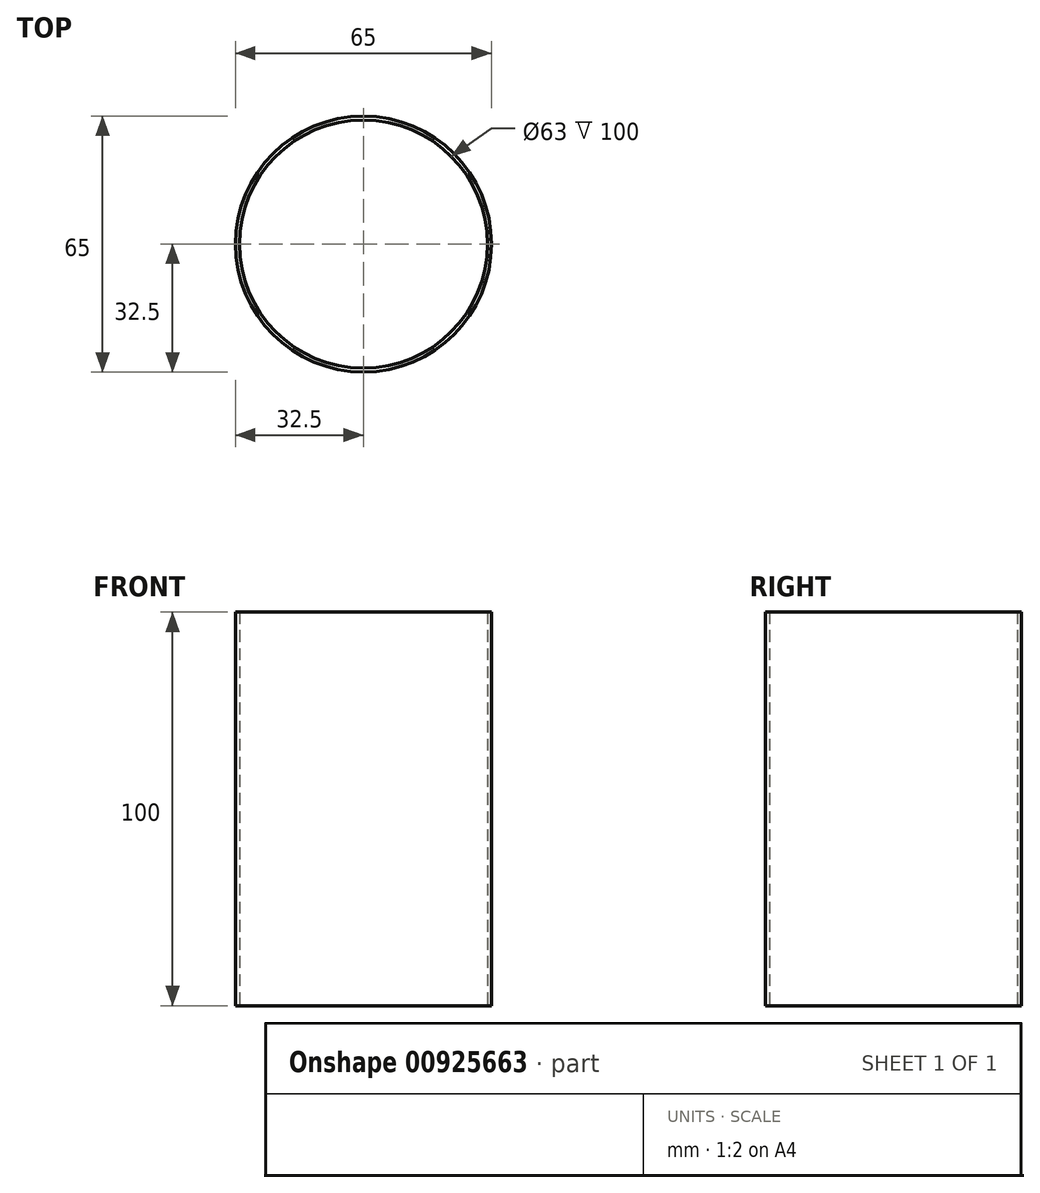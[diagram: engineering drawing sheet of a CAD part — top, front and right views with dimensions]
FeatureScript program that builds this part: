
annotation { "Feature Type Name" : "Feature", "Feature Type Description" : "" }
export const myFeature = defineFeature(function(context is Context, id is Id, definition is map)
    precondition{}
    {
        {
            var Q0;
            Q0=qCreatedBy(makeId("Top.planeOp"),FACE);
            var sketch = newSketch(context, id + "F0", { "sketchPlane" : qUnion([Q0])});
            skCircle(sketch, "E0", {"center": v(0, 0) * mm, "radius": 32.5 * mm});
            skCircle(sketch, "E1", {"center": v(0, 0) * mm, "radius": 31.5 * mm});
            skSolve(sketch);
        }
        {
            var Q0;
            Q0=makeQuery(id+"F0.imprint","IMPRINT",FACE,{"disambiguationData":[TD([[makeQuery(id+"F0.imprint","IMPRINT",EDGE,{"derivedFrom":sQuery(id+"F0.wireOp",EDGE,"E0")}),1.0]])]});
            extrude(context, id + "F1", {"entities" : qUnion([Q0]), "endBound" : BoundingType.SYMMETRIC, "depth" : 100 * mm, "offsetDistance" : 25 * mm});
        }
    });
